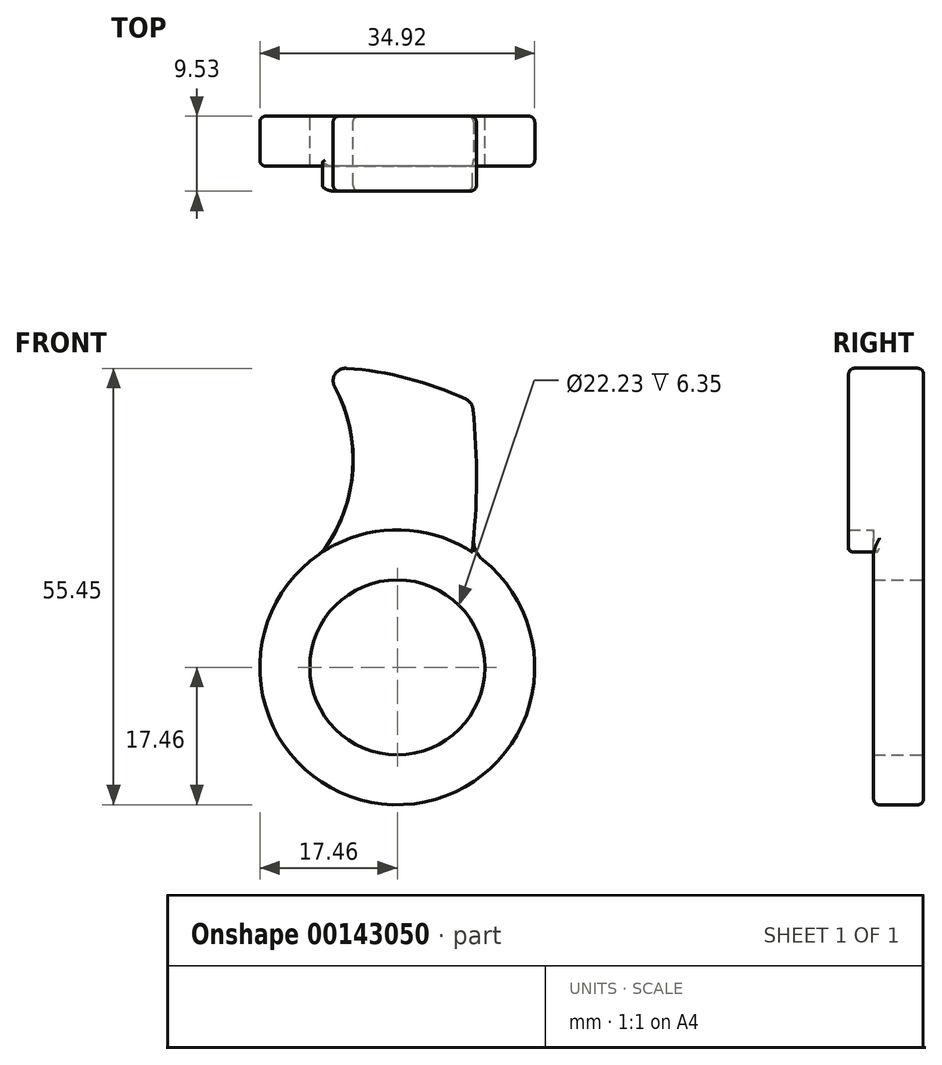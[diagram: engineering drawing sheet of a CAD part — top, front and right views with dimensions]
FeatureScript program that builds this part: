
annotation { "Feature Type Name" : "Feature", "Feature Type Description" : "" }
export const myFeature = defineFeature(function(context is Context, id is Id, definition is map)
    precondition{}
    {
        {
            var Q0;
            Q0=qCreatedBy(makeId("Front.planeOp"),FACE);
            var sketch = newSketch(context, id + "F0", { "sketchPlane" : qUnion([Q0])});
            skCircle(sketch, "E0", {"center": v(0, 0) * mm, "radius": 11.11 * mm});
            skCircle(sketch, "E1", {"center": v(0, 0) * mm, "radius": 17.46 * mm});
            skLineSegment(sketch, "E2", {"start": v(0, 0) * mm, "end": v(0, 38.1) * mm, "construction": true});
            skLineSegment(sketch, "E3", {"start": v(-9.52, 14.64) * mm, "end": v(-9.52, 38.1) * mm, "construction": true});
            skLineSegment(sketch, "E4", {"start": v(-9.53, 38.1) * mm, "end": v(9.53, 38.1) * mm, "construction": true});
            skLineSegment(sketch, "E5", {"start": v(9.53, 38.1) * mm, "end": v(9.53, 14.64) * mm, "construction": true});
            skPoint(sketch, "E6.1.internal.snap0", {"position": v(-9.52, 26.37) * mm});
            skPoint(sketch, "E7", {"position": v(9.53, 26.37) * mm});
            skArc(sketch, "E8", {"start": v(-9.52, 14.64) * mm, "mid": v(-5.66, 24.91) * mm, "end": v(-7.95, 35.65) * mm});
            skArc(sketch, "E9", {"start": v(8.71, 34.06) * mm, "mid": v(1.31, 36.72) * mm, "end": v(-6.44, 37.99) * mm});
            skArc(sketch, "E10", {"start": v(9.53, 14.64) * mm, "mid": v(10.06, 23.7) * mm, "end": v(9.62, 32.78) * mm});
            skPoint(sketch, "E11.visualSharp", {"position": v(-9.52, 38.1) * mm});
            skArc(sketch, "E11.filletArc", {"start": v(-6.44, 37.99) * mm, "mid": v(-7.9, 37.27) * mm, "end": v(-7.95, 35.65) * mm});
            skPoint(sketch, "E12.visualSharp", {"position": v(9.53, 33.67) * mm});
            skArc(sketch, "E12.filletArc", {"start": v(9.62, 32.78) * mm, "mid": v(9.33, 33.54) * mm, "end": v(8.71, 34.06) * mm});
            skSolve(sketch);
        }
        {
            var Q0;
            Q0=makeQuery(id+"F0.imprint","IMPRINT",FACE,{"disambiguationData":[TD([[makeQuery(id+"F0.imprint","IMPRINT",EDGE,{"derivedFrom":sQuery(id+"F0.wireOp",EDGE,"E0")}),-1.0]])]});
            var Q1;
            {var subQ1=sQuery(id+"F0.wireOp",EDGE,"E8");Q1=makeQuery(id+"F0.imprint","IMPRINT",FACE,{"disambiguationData":[TD([[makeQuery(id+"F0.imprint","IMPRINT",EDGE,{"derivedFrom":subQ1}),-1.0]])]});}
            extrude(context, id + "F1", {"entities" : qUnion([Q0, Q1]), "depth" : 6.35 * mm});
        }
        {
            var Q0;
            Q0=makeQuery(id+"F1.opExtrude","SWEPT_EDGE",EDGE,{"disambiguationData":[OSD([sQuery(id+"F0.wireOp",EDGE,"E1"),sQuery(id+"F0.wireOp",EDGE,"E10")])]});
            var Q1;
            Q1=makeQuery(id+"F1.opExtrude","SWEPT_EDGE",EDGE,{"disambiguationData":[OSD([sQuery(id+"F0.wireOp",EDGE,"E1"),sQuery(id+"F0.wireOp",EDGE,"E8")])]});
            fillet(context, id + "F2", {"entities" : qUnion([Q0, Q1]), "radius" : 3.17 * mm, "tangentPropagation" : true, "allowEdgeOverflow" : false});
        }
        {
            var Q0;
            {var subQ1=sQuery(id+"F0.wireOp",EDGE,"E8");Q0=makeQuery(id+"F0.imprint","IMPRINT",FACE,{"disambiguationData":[TD([[makeQuery(id+"F0.imprint","IMPRINT",EDGE,{"derivedFrom":subQ1}),-1.0]])]});}
            extrude(context, id + "F3", {"entities" : qUnion([Q0]), "operationType" : NewBodyOperationType.ADD, "depth" : 9.52 * mm});
        }
        {
            var Q0;
            Q0=makeQuery(id+"F3.opExtrude","CAP_EDGE",EDGE,{"disambiguationData":[OSD([sQuery(id+"F0.wireOp",EDGE,"E10")])],"isStart":false});
            fillet(context, id + "F4", {"entities" : qUnion([Q0]), "radius" : 0.76 * mm, "tangentPropagation" : true, "allowEdgeOverflow" : false});
        }
        {
            var Q0;
            Q0=makeQuery(id+"F1.opExtrude","CAP_EDGE",EDGE,{"disambiguationData":[OSD([sQuery(id+"F0.wireOp",EDGE,"E1")])],"isStart":false});
            var Q1;
            Q1=makeQuery(id+"F1.opExtrude","CAP_EDGE",EDGE,{"disambiguationData":[OSD([sQuery(id+"F0.wireOp",EDGE,"E1")])],"isStart":true});
            fillet(context, id + "F5", {"entities" : qUnion([Q0, Q1]), "radius" : 0.76 * mm, "tangentPropagation" : true, "allowEdgeOverflow" : false});
        }
    });
